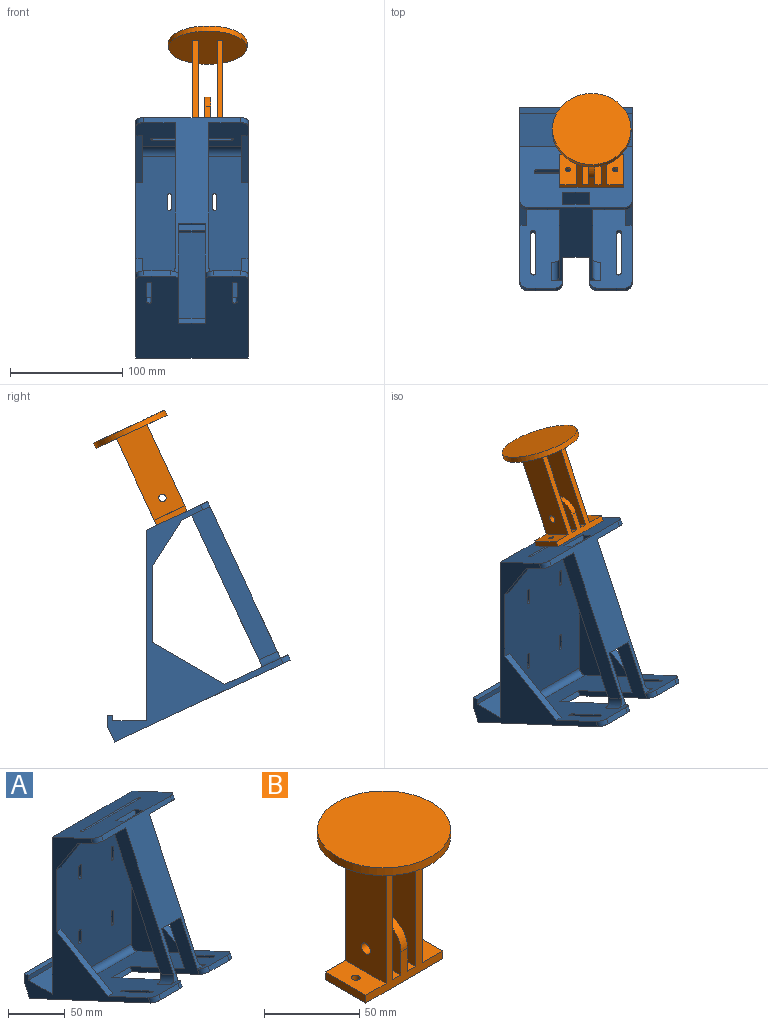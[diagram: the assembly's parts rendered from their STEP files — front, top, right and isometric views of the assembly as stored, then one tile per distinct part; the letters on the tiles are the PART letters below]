
ASSEMBLY  parts=2 mates=1
PART A: 72 faces, bbox 100x163.1x214.2 mm
  f0: plane 24x4.53mm, normal (0,-0.91,0.42), area 120mm2, adj f3,f5,f65,f70
  f1: plane 135.11x63mm, normal (0,0.91,-0.42), area 3293.2mm2, adj f3,f12,f55,f56,f58,f60,f61,f66
  f2: plane 100x54.38mm, normal (0,0.42,0.91), area 5390.8mm2, adj f10,f11,f17,f18,f51,f52,f53,f54
  f3: plane 113.91x100mm, normal (0,0.42,0.91), area 8647.7mm2, adj f0,f1,f6,f11,f14,f15,f17,f18
  f4: plane 42.17x26.87mm, normal (0,-0.84,-0.54), area 300mm2, adj f12,f13,f18,f48
  f5: plane 156.62x100mm, normal (0,-0.42,-0.91), area 14485.1mm2, adj f0,f15,f17,f18,f21,f22,f23,f24
  f6: plane 64.84x37.43mm, normal (0,-0.5,0.87), area 449.2mm2, adj f3,f13,f17,f19
  f7: plane 100x5mm, normal (0,0,1), area 500mm2, adj f8,f16,f17,f18
  f8: plane 100x5mm, normal (0,-1,0), area 500mm2, adj f7,f9,f17,f18
  f9: plane 100x30mm, normal (0,0,1), area 3000mm2, adj f8,f10,f17,f18
  f10: plane 170x100mm, normal (0,1,0), area 16811mm2, adj f2,f9,f17,f18,f31,f32,f33,f34
  f11: plane 139.64x86mm, normal (0,-0.91,0.42), area 3723.2mm2, adj f2,f3,f12,f55,f56,f58,f60,f62
  f12: plane 100x45.72mm, normal (0,-0.42,-0.91), area 3903.9mm2, adj f1,f4,f11,f17,f18,f47,f48,f49
  f13: plane 150.26x100mm, normal (0,-1,0), area 13840.3mm2, adj f4,f6,f14,f17,f18,f19,f20,f30
  f14: plane 64.84x37.43mm, normal (0,-0.5,0.87), area 449.2mm2, adj f3,f13,f18,f20
  f15: plane 24x4.53mm, normal (0,-0.91,0.42), area 120mm2, adj f3,f5,f64,f68
  f16: plane 100x9.84mm, normal (0,1,0), area 983.8mm2, adj f7,f17,f18,f21
  f17: plane 211.2x156.79mm, normal (1,0,0), area 4799.6mm2, adj f2,f3,f5,f6,f7,f8,f9,f10
  f18: plane 211.2x156.79mm, normal (-1,0,0), area 4799.6mm2, adj f2,f3,f4,f5,f7,f8,f9,f10
  f19: plane 64.84x64.82mm, normal (-1,0,0), area 2179.6mm2, adj f3,f6,f13,f30
  f20: plane 64.84x64.82mm, normal (1,0,0), area 2179.6mm2, adj f3,f13,f14,f30
  f21: plane 100x13.96mm, normal (0,0.91,-0.42), area 1540.7mm2, adj f5,f16,f17,f18
  f22: cylinder r=2.05mm len=5.4mm, axis (0,0.42,0.91), area 32.2mm2, adj f3,f5,f23,f25
  f23: plane 38.37x21.44mm, normal (1,0,0), area 200mm2, adj f3,f5,f22,f24
  f24: cylinder r=2.05mm len=5.4mm, axis (0,0.42,0.91), area 32.2mm2, adj f3,f5,f23,f25
  f25: plane 38.37x21.44mm, normal (-1,0,0), area 200mm2, adj f3,f5,f22,f24
  f26: plane 38.37x21.44mm, normal (1,0,0), area 200mm2, adj f3,f5,f27,f29
  f27: cylinder r=2.05mm len=5.4mm, axis (0,0.42,0.91), area 32.2mm2, adj f3,f5,f26,f28
  f28: plane 38.37x21.44mm, normal (-1,0,0), area 200mm2, adj f3,f5,f27,f29
  f29: cylinder r=2.05mm len=5.4mm, axis (0,0.42,0.91), area 32.2mm2, adj f3,f5,f26,f28
  f30: cylinder r=5mm len=88mm, axis (1,0,0), area 883.1mm2, adj f3,f13,f19,f20
  f31: cylinder r=1.6mm len=5mm, axis (0,1,0), area 25.1mm2, adj f10,f13,f32,f33
  f32: plane 12.5x5mm, normal (1,0,0), area 62.5mm2, adj f10,f13,f31,f34
  f33: plane 12.5x5mm, normal (-1,0,0), area 62.5mm2, adj f10,f13,f31,f34
  f34: cylinder r=1.6mm len=5mm, axis (0,1,0), area 25.1mm2, adj f10,f13,f32,f33
  f35: cylinder r=1.6mm len=5mm, axis (0,1,0), area 25.1mm2, adj f10,f13,f36,f37
  f36: plane 12x5mm, normal (1,0,0), area 60mm2, adj f10,f13,f35,f38
  f37: plane 12x5mm, normal (-1,0,0), area 60mm2, adj f10,f13,f35,f38
  f38: cylinder r=1.6mm len=5mm, axis (0,1,0), area 25.1mm2, adj f10,f13,f36,f37
  f39: cylinder r=1.6mm len=5mm, axis (0,1,0), area 25.1mm2, adj f10,f13,f40,f41
  f40: plane 12x5mm, normal (1,0,0), area 60mm2, adj f10,f13,f39,f42
  f41: plane 12x5mm, normal (-1,0,0), area 60mm2, adj f10,f13,f39,f42
  f42: cylinder r=1.6mm len=5mm, axis (0,1,0), area 25.1mm2, adj f10,f13,f40,f41
  f43: cylinder r=1.6mm len=5mm, axis (0,1,0), area 25.1mm2, adj f10,f13,f44,f45
  f44: plane 12.5x5mm, normal (-1,0,0), area 62.5mm2, adj f10,f13,f43,f46
  f45: plane 12.5x5mm, normal (1,0,0), area 62.5mm2, adj f10,f13,f43,f46
  f46: cylinder r=1.6mm len=5mm, axis (0,1,0), area 25.1mm2, adj f10,f13,f44,f45
  f47: plane 42.17x26.87mm, normal (0,-0.84,-0.54), area 300mm2, adj f12,f13,f17,f49
  f48: plane 42.17x26.87mm, normal (1,0,0), area 391.2mm2, adj f4,f12,f13,f50
  f49: plane 42.17x26.87mm, normal (-1,0,0), area 391.2mm2, adj f12,f13,f47,f50
  f50: cylinder r=10mm len=88mm, axis (1,0,0), area 998.3mm2, adj f12,f13,f48,f49
  f51: cylinder r=2.05mm len=6.26mm, axis (0,0.42,0.91), area 32.2mm2, adj f2,f12,f52,f53
  f52: plane 70x4.53mm, normal (0,-0.91,0.42), area 350mm2, adj f2,f12,f51,f54
  f53: plane 70x4.53mm, normal (0,0.91,-0.42), area 350mm2, adj f2,f12,f51,f54
  f54: cylinder r=2.05mm len=6.26mm, axis (0,0.42,0.91), area 32.2mm2, adj f2,f12,f52,f53
  f55: plane 136.37x76.36mm, normal (1,0,0), area 2557.3mm2, adj f1,f11,f12,f67
  f56: plane 136.37x76.36mm, normal (-1,0,0), area 2557.3mm2, adj f1,f11,f12,f66
  f57: plane 94.32x43.98mm, normal (0,0.91,-0.42), area 2497.7mm2, adj f2,f58,f60,f62
  f58: plane 182.12x86.4mm, normal (-1,0,0), area 2613.9mm2, adj f1,f2,f3,f5,f11,f57,f59,f61
  f59: plane 94.32x43.98mm, normal (0,-0.91,0.42), area 2497.7mm2, adj f2,f58,f60,f61
  f60: plane 182.12x86.4mm, normal (1,0,0), area 2613.9mm2, adj f1,f2,f3,f5,f11,f57,f59,f61
  f61: plane 24x2.72mm, normal (0,-0.42,-0.91), area 72mm2, adj f1,f58,f59,f60
  f62: plane 24x2.72mm, normal (0,-0.42,-0.91), area 72mm2, adj f11,f57,f58,f60
  f63: plane 24x4.53mm, normal (0,-0.91,0.42), area 120mm2, adj f3,f5,f58,f60
  f64: cylinder r=7mm len=8.46mm, axis (0,-0.42,-0.91), area 55mm2, adj f3,f5,f15,f60
  f65: cylinder r=7mm len=8.46mm, axis (0,0.42,0.91), area 55mm2, adj f0,f3,f5,f58
  f66: cylinder r=7mm len=19.27mm, axis (0,-0.91,0.42), area 197.9mm2, adj f1,f3,f11,f56
  f67: cylinder r=7mm len=19.27mm, axis (0,0.91,-0.42), area 197.9mm2, adj f1,f3,f11,f55
  f68: cylinder r=7mm len=8.46mm, axis (0,-0.42,-0.91), area 55mm2, adj f3,f5,f15,f18
  f69: cylinder r=7mm len=8.46mm, axis (0,-0.42,-0.91), area 55mm2, adj f2,f11,f12,f18
  f70: cylinder r=7mm len=8.46mm, axis (0,0.42,0.91), area 55mm2, adj f0,f3,f5,f17
  f71: cylinder r=7mm len=8.46mm, axis (0,0.42,0.91), area 55mm2, adj f2,f11,f12,f17
PART B: 29 faces, bbox 70x70x90 mm
  f0: plane 80x30mm, normal (-1,0,0), area 2365.8mm2, adj f5,f6,f12,f20,f26
  f1: plane 80x30mm, normal (1,0,0), area 2306.5mm2, adj f5,f6,f13,f14,f15,f16,f17,f18
  f2: plane 30x30mm, normal (1,0,0), area 769.2mm2, adj f5,f6,f8,f11,f19
  f3: plane 30x30mm, normal (-1,0,0), area 769.2mm2, adj f5,f6,f10,f11,f19
  f4: plane 80x30mm, normal (-1,0,0), area 2306.5mm2, adj f5,f6,f8,f13,f14,f15,f16,f17
  f5: plane 85x57mm, normal (0,1,0), area 1160mm2, adj f0,f1,f2,f3,f4,f7,f8,f9
  f6: plane 85x57mm, normal (0,-1,0), area 1160mm2, adj f0,f1,f2,f3,f4,f7,f8,f9
  f7: plane 57x30mm, normal (0,0,-1), area 1678.2mm2, adj f5,f6,f24,f25,f27,f28
  f8: plane 30x6mm, normal (0,0,1), area 180mm2, adj f2,f4,f5,f6
  f9: plane 80x30mm, normal (1,0,0), area 2365.8mm2, adj f5,f6,f10,f12,f20
  f10: plane 30x6mm, normal (0,0,1), area 180mm2, adj f3,f5,f6,f9
  f11: cylinder r=3.3mm len=6.6mm, axis (1,0,0), area 103.7mm2, adj f2,f3
  f12: cylinder r=3.3mm len=6.6mm, axis (1,0,0), area 103.7mm2, adj f0,f9
  f13: plane 6x5mm, normal (0,-1,0), area 30mm2, adj f1,f4,f14,f18
  f14: plane 5.2x5mm, normal (0,-0.5,0.87), area 30mm2, adj f1,f4,f13,f15
  f15: plane 5.2x5mm, normal (0,0.5,0.87), area 30mm2, adj f1,f4,f14,f16
  f16: plane 6x5mm, normal (0,1,0), area 30mm2, adj f1,f4,f15,f17
  f17: plane 5.2x5mm, normal (0,0.5,-0.87), area 30mm2, adj f1,f4,f16,f18
  f18: plane 5.2x5mm, normal (0,-0.5,-0.87), area 30mm2, adj f1,f4,f13,f17
  f19: cylinder r=15mm len=30mm, axis (1,0,0), area 235.6mm2, adj f2,f3,f5,f6
  f20: plane 70x70mm, normal (0,0,-1), area 3548.5mm2, adj f0,f1,f4,f5,f6,f9,f21
  f21: cylinder r=35mm len=70mm, axis (0,0,-1), area 1099.6mm2, adj f20,f22
  f22: plane 70x70mm, normal (0,0,1), area 3848.5mm2, adj f21
  f23: plane 30x15mm, normal (0,0,1), area 434.1mm2, adj f1,f5,f6,f24,f25
  f24: plane 30x5mm, normal (1,0,0), area 150mm2, adj f5,f6,f7,f23
  f25: cylinder r=2.25mm len=5mm, axis (0,0,1), area 70.7mm2, adj f7,f23
  f26: plane 30x15mm, normal (0,0,1), area 434.1mm2, adj f0,f5,f6,f27,f28
  f27: plane 30x5mm, normal (-1,0,0), area 150mm2, adj f5,f6,f7,f26
  f28: cylinder r=2.25mm len=5mm, axis (0,0,1), area 70.7mm2, adj f7,f26
PLACE A t=(-0.64,41.33,-18.07)mm
PLACE B rot(axis=(-1,0,0),25deg) t=(13.36,41.64,131.01)mm
MATE fastened B.f25 <-> A.f54  axis (0,-0.42,-0.91) through (34.36,23.68,92.49)mm
